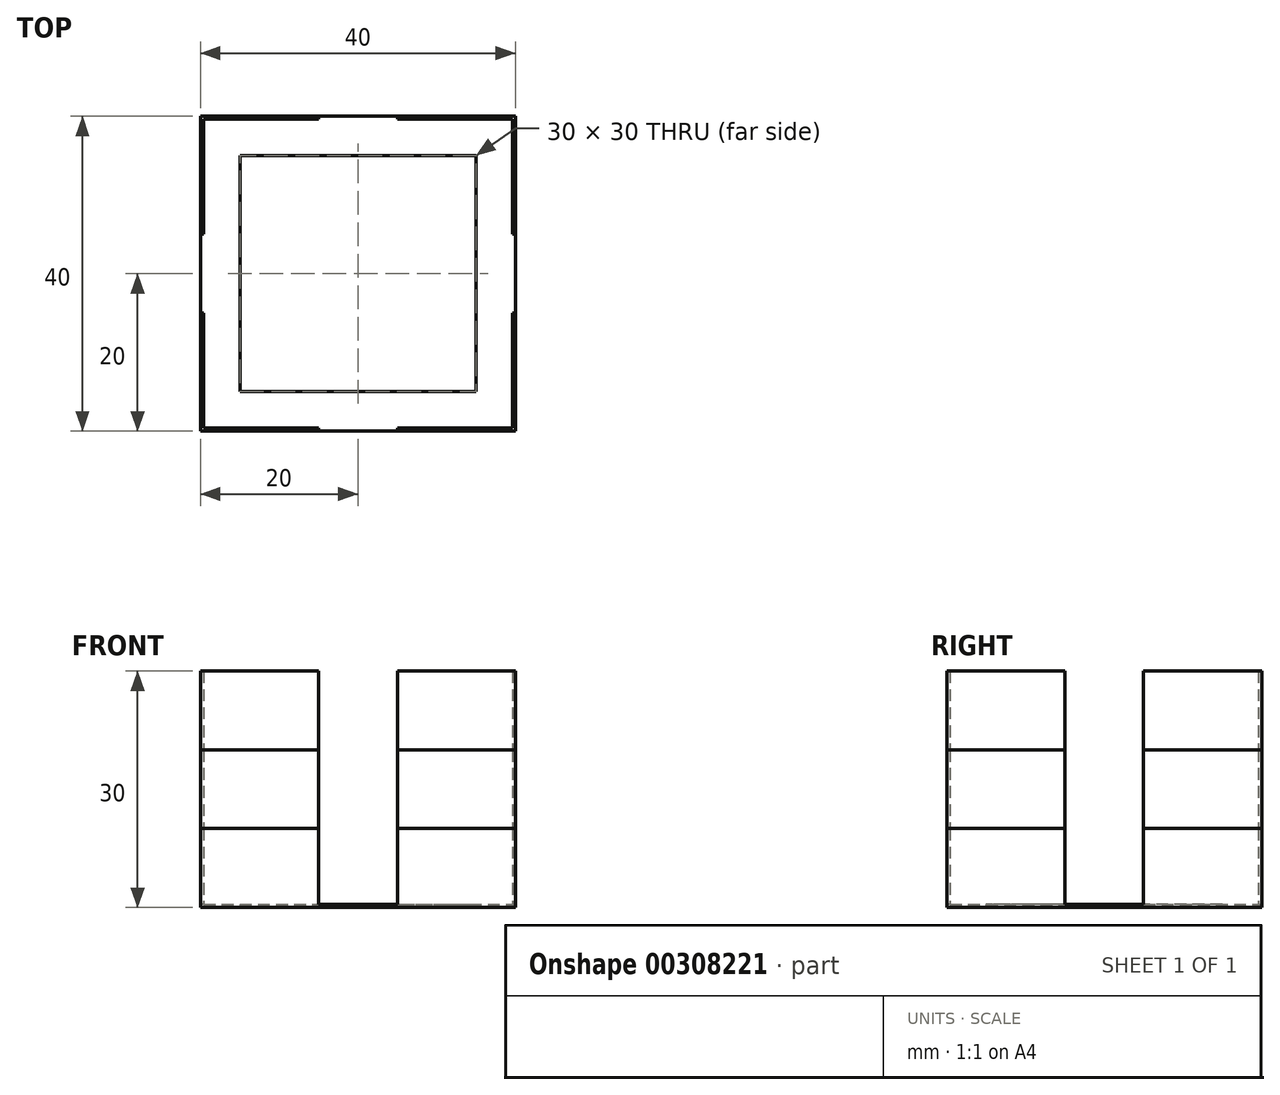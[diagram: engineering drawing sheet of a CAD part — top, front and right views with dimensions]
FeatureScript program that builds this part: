
annotation { "Feature Type Name" : "Feature", "Feature Type Description" : "" }
export const myFeature = defineFeature(function(context is Context, id is Id, definition is map)
    precondition{}
    {
        {
            assignVariable(context, id + "F0", {"name" : "thick_bottom", "anyValue" : .4});
        }
        {
            var Q0;
            Q0=qCreatedBy(makeId("Top.planeOp"),FACE);
            var sketch = newSketch(context, id + "F1", { "sketchPlane" : qUnion([Q0])});
            skLineSegment(sketch, "E0.bottom", {"start": v(-20, 20) * mm, "end": v(-5, 20) * mm});
            skLineSegment(sketch, "E0.top", {"start": v(-20, -20) * mm, "end": v(-5, -20) * mm});
            skLineSegment(sketch, "E0.left", {"start": v(-20, 20) * mm, "end": v(-20, 5) * mm});
            skLineSegment(sketch, "E0.right", {"start": v(20, 20) * mm, "end": v(20, 5) * mm});
            skPoint(sketch, "E0.middle", {"position": v(0, 0) * mm});
            skLineSegment(sketch, "E1", {"start": v(20, -5) * mm, "end": v(20, -20) * mm});
            skLineSegment(sketch, "E2", {"start": v(20, 5) * mm, "end": v(20, -5) * mm});
            skLineSegment(sketch, "E3", {"start": v(5, 20) * mm, "end": v(20, 20) * mm});
            skLineSegment(sketch, "E4", {"start": v(-5, 20) * mm, "end": v(5, 20) * mm});
            skLineSegment(sketch, "E5", {"start": v(-20, 5) * mm, "end": v(-20, -5) * mm});
            skLineSegment(sketch, "E6", {"start": v(-20, -5) * mm, "end": v(-20, -20) * mm});
            skLineSegment(sketch, "E7", {"start": v(-5, -20) * mm, "end": v(5, -20) * mm});
            skLineSegment(sketch, "E8", {"start": v(5, -20) * mm, "end": v(20, -20) * mm});
            skLineSegment(sketch, "E9", {"start": v(20, -5) * mm, "end": v(19.6, -5) * mm});
            skLineSegment(sketch, "E10", {"start": v(19.6, -5) * mm, "end": v(19.6, -19.6) * mm});
            skLineSegment(sketch, "E11", {"start": v(19.6, -19.6) * mm, "end": v(5, -19.6) * mm});
            skLineSegment(sketch, "E12", {"start": v(5, -19.6) * mm, "end": v(5, -20) * mm});
            skLineSegment(sketch, "E13", {"start": v(-5, -20) * mm, "end": v(-5, -19.6) * mm});
            skLineSegment(sketch, "E14", {"start": v(-5, -19.6) * mm, "end": v(-19.6, -19.6) * mm});
            skLineSegment(sketch, "E15", {"start": v(-19.6, -19.6) * mm, "end": v(-19.6, -5) * mm});
            skLineSegment(sketch, "E16", {"start": v(-19.6, -5) * mm, "end": v(-20, -5) * mm});
            skLineSegment(sketch, "E17", {"start": v(-20, 5) * mm, "end": v(-19.6, 5) * mm});
            skLineSegment(sketch, "E18", {"start": v(-19.6, 5) * mm, "end": v(-19.6, 19.6) * mm});
            skLineSegment(sketch, "E19", {"start": v(-19.6, 19.6) * mm, "end": v(-5, 19.6) * mm});
            skLineSegment(sketch, "E20", {"start": v(-5, 19.6) * mm, "end": v(-5, 20) * mm});
            skLineSegment(sketch, "E21", {"start": v(5, 20) * mm, "end": v(5, 19.6) * mm});
            skLineSegment(sketch, "E22", {"start": v(5, 19.6) * mm, "end": v(19.6, 19.6) * mm});
            skLineSegment(sketch, "E23", {"start": v(19.6, 19.6) * mm, "end": v(19.6, 5) * mm});
            skLineSegment(sketch, "E24", {"start": v(19.6, 5) * mm, "end": v(20, 5) * mm});
            skLineSegment(sketch, "E25.bottom", {"start": v(-15, 15) * mm, "end": v(15, 15) * mm});
            skLineSegment(sketch, "E25.top", {"start": v(-15, -15) * mm, "end": v(15, -15) * mm});
            skLineSegment(sketch, "E25.left", {"start": v(-15, 15) * mm, "end": v(-15, -15) * mm});
            skLineSegment(sketch, "E25.right", {"start": v(15, 15) * mm, "end": v(15, -15) * mm});
            skSolve(sketch);
        }
        {
            var Q0;
            Q0=makeQuery(id+"F1.imprint","IMPRINT",FACE,{"disambiguationData":[TD([[makeQuery(id+"F1.imprint","IMPRINT",EDGE,{"derivedFrom":sQuery(id+"F1.wireOp",EDGE,"E0.bottom")}),-1.0]])]});
            var Q1;
            Q1=makeQuery(id+"F1.imprint","IMPRINT",FACE,{"disambiguationData":[TD([[makeQuery(id+"F1.imprint","IMPRINT",EDGE,{"derivedFrom":sQuery(id+"F1.wireOp",EDGE,"E0.right")}),-1.0]])]});
            var Q2;
            Q2=makeQuery(id+"F1.imprint","IMPRINT",FACE,{"disambiguationData":[TD([[makeQuery(id+"F1.imprint","IMPRINT",EDGE,{"derivedFrom":sQuery(id+"F1.wireOp",EDGE,"E2")}),-1.0]])]});
            var Q3;
            Q3=makeQuery(id+"F1.imprint","IMPRINT",FACE,{"disambiguationData":[TD([[makeQuery(id+"F1.imprint","IMPRINT",EDGE,{"derivedFrom":sQuery(id+"F1.wireOp",EDGE,"E1")}),-1.0]])]});
            var Q4;
            Q4=makeQuery(id+"F1.imprint","IMPRINT",FACE,{"disambiguationData":[TD([[makeQuery(id+"F1.imprint","IMPRINT",EDGE,{"derivedFrom":sQuery(id+"F1.wireOp",EDGE,"E0.top")}),1.0]])]});
            extrude(context, id + "F2", {"entities" : qUnion([Q0, Q1, Q2, Q3, Q4]), "depth" : (getVariable(context, 'thick_bottom')) * mm, "offsetDistance" : 25 * mm});
        }
        {
            var Q0;
            Q0=makeQuery(id+"F1.imprint","IMPRINT",FACE,{"disambiguationData":[TD([[makeQuery(id+"F1.imprint","IMPRINT",EDGE,{"derivedFrom":sQuery(id+"F1.wireOp",EDGE,"E1")}),-1.0]])]});
            var Q1;
            Q1=makeQuery(id+"F1.imprint","IMPRINT",FACE,{"disambiguationData":[TD([[makeQuery(id+"F1.imprint","IMPRINT",EDGE,{"derivedFrom":sQuery(id+"F1.wireOp",EDGE,"E0.top")}),1.0]])]});
            var Q2;
            Q2=makeQuery(id+"F1.imprint","IMPRINT",FACE,{"disambiguationData":[TD([[makeQuery(id+"F1.imprint","IMPRINT",EDGE,{"derivedFrom":sQuery(id+"F1.wireOp",EDGE,"E0.right")}),-1.0]])]});
            var Q3;
            Q3=makeQuery(id+"F1.imprint","IMPRINT",FACE,{"disambiguationData":[TD([[makeQuery(id+"F1.imprint","IMPRINT",EDGE,{"derivedFrom":sQuery(id+"F1.wireOp",EDGE,"E0.bottom")}),-1.0]])]});
            extrude(context, id + "F3", {"entities" : qUnion([Q0, Q1, Q2, Q3]), "operationType" : NewBodyOperationType.ADD, "depth" : 10 * mm, "offsetDistance" : 25 * mm});
        }
        {
            var Q0;
            Q0=makeQuery(id+"F3.opExtrude","CAP_FACE",FACE,{"disambiguationData":[OSD([sQuery(id+"F1.wireOp",EDGE,"E0.bottom"),sQuery(id+"F1.wireOp",EDGE,"E0.left"),sQuery(id+"F1.wireOp",EDGE,"E17"),sQuery(id+"F1.wireOp",EDGE,"E18"),sQuery(id+"F1.wireOp",EDGE,"E19"),sQuery(id+"F1.wireOp",EDGE,"E20")])],"isStart":false});
            var Q1;
            Q1=makeQuery(id+"F3.opExtrude","CAP_FACE",FACE,{"disambiguationData":[OSD([sQuery(id+"F1.wireOp",EDGE,"E0.right"),sQuery(id+"F1.wireOp",EDGE,"E3"),sQuery(id+"F1.wireOp",EDGE,"E21"),sQuery(id+"F1.wireOp",EDGE,"E22"),sQuery(id+"F1.wireOp",EDGE,"E23"),sQuery(id+"F1.wireOp",EDGE,"E24")])],"isStart":false});
            var Q2;
            Q2=makeQuery(id+"F3.opExtrude","CAP_FACE",FACE,{"disambiguationData":[OSD([sQuery(id+"F1.wireOp",EDGE,"E1"),sQuery(id+"F1.wireOp",EDGE,"E8"),sQuery(id+"F1.wireOp",EDGE,"E9"),sQuery(id+"F1.wireOp",EDGE,"E10"),sQuery(id+"F1.wireOp",EDGE,"E11"),sQuery(id+"F1.wireOp",EDGE,"E12")])],"isStart":false});
            var Q3;
            Q3=makeQuery(id+"F3.opExtrude","CAP_FACE",FACE,{"disambiguationData":[OSD([sQuery(id+"F1.wireOp",EDGE,"E0.top"),sQuery(id+"F1.wireOp",EDGE,"E6"),sQuery(id+"F1.wireOp",EDGE,"E13"),sQuery(id+"F1.wireOp",EDGE,"E14"),sQuery(id+"F1.wireOp",EDGE,"E15"),sQuery(id+"F1.wireOp",EDGE,"E16")])],"isStart":false});
            extrude(context, id + "F4", {"entities" : qUnion([Q0, Q1, Q2, Q3]), "depth" : 10 * mm, "offsetDistance" : 25 * mm});
        }
        {
            var Q0;
            Q0=makeQuery(id+"F4.opExtrude","CAP_FACE",FACE,{"disambiguationData":[OSD([sQuery(id+"F1.wireOp",EDGE,"E0.bottom"),sQuery(id+"F1.wireOp",EDGE,"E0.left"),sQuery(id+"F1.wireOp",EDGE,"E17"),sQuery(id+"F1.wireOp",EDGE,"E18"),sQuery(id+"F1.wireOp",EDGE,"E19"),sQuery(id+"F1.wireOp",EDGE,"E20")])],"isStart":false});
            var Q1;
            Q1=makeQuery(id+"F4.opExtrude","CAP_FACE",FACE,{"disambiguationData":[OSD([sQuery(id+"F1.wireOp",EDGE,"E0.right"),sQuery(id+"F1.wireOp",EDGE,"E3"),sQuery(id+"F1.wireOp",EDGE,"E21"),sQuery(id+"F1.wireOp",EDGE,"E22"),sQuery(id+"F1.wireOp",EDGE,"E23"),sQuery(id+"F1.wireOp",EDGE,"E24")])],"isStart":false});
            var Q2;
            Q2=makeQuery(id+"F4.opExtrude","CAP_FACE",FACE,{"disambiguationData":[OSD([sQuery(id+"F1.wireOp",EDGE,"E1"),sQuery(id+"F1.wireOp",EDGE,"E8"),sQuery(id+"F1.wireOp",EDGE,"E9"),sQuery(id+"F1.wireOp",EDGE,"E10"),sQuery(id+"F1.wireOp",EDGE,"E11"),sQuery(id+"F1.wireOp",EDGE,"E12")])],"isStart":false});
            var Q3;
            Q3=makeQuery(id+"F4.opExtrude","CAP_FACE",FACE,{"disambiguationData":[OSD([sQuery(id+"F1.wireOp",EDGE,"E0.top"),sQuery(id+"F1.wireOp",EDGE,"E6"),sQuery(id+"F1.wireOp",EDGE,"E13"),sQuery(id+"F1.wireOp",EDGE,"E14"),sQuery(id+"F1.wireOp",EDGE,"E15"),sQuery(id+"F1.wireOp",EDGE,"E16")])],"isStart":false});
            extrude(context, id + "F5", {"entities" : qUnion([Q0, Q1, Q2, Q3]), "depth" : 10 * mm, "offsetDistance" : 25 * mm});
        }
    });
